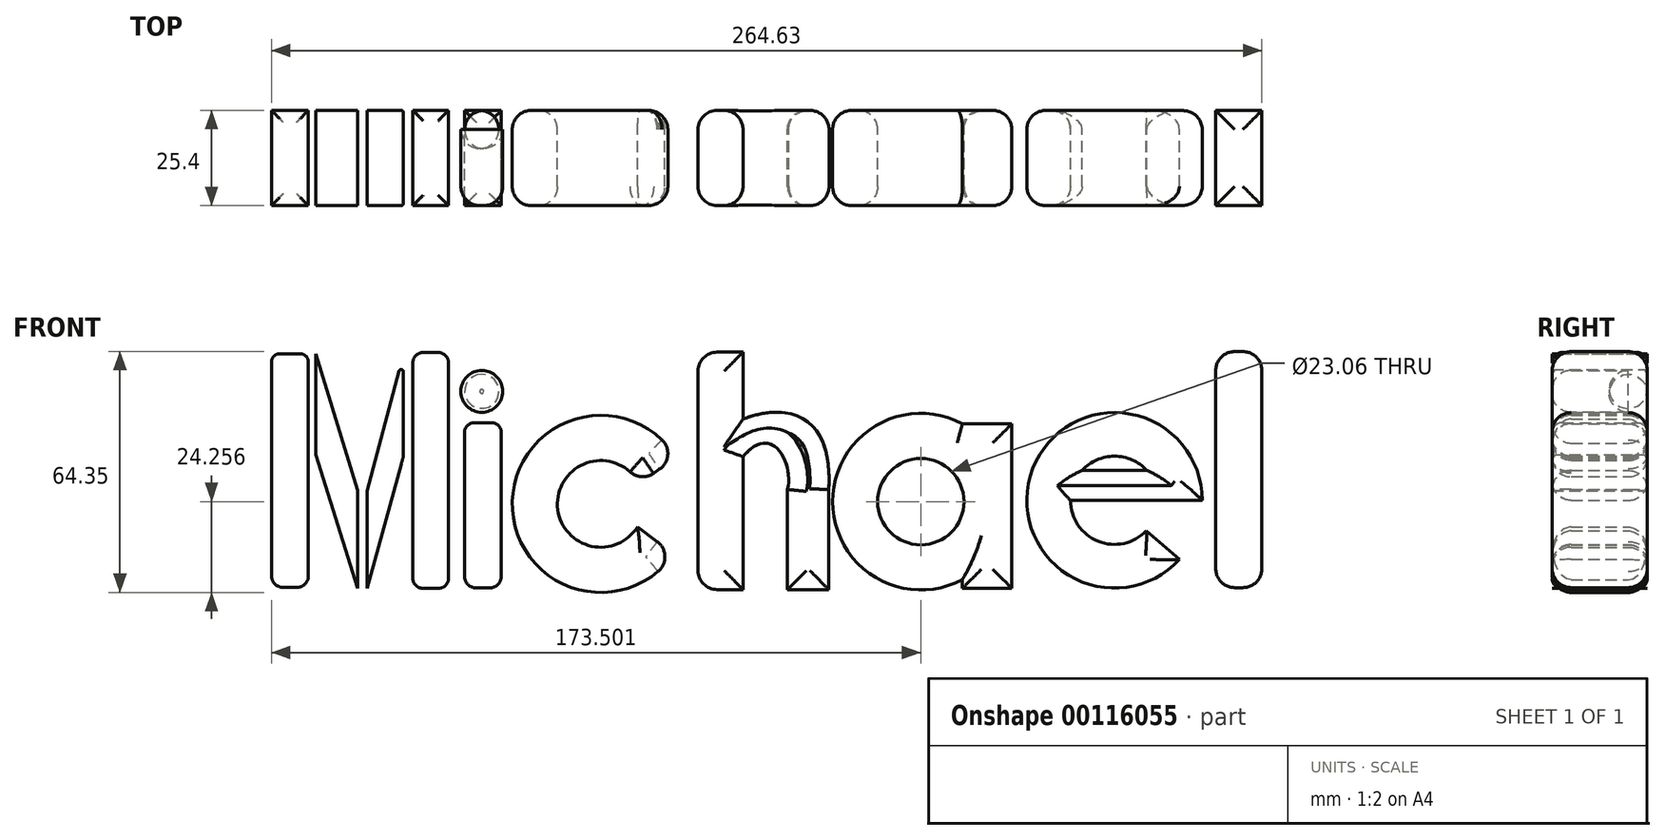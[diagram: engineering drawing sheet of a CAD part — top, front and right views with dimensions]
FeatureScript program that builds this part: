
annotation { "Feature Type Name" : "Feature", "Feature Type Description" : "" }
export const myFeature = defineFeature(function(context is Context, id is Id, definition is map)
    precondition{}
    {
        {
            var Q0;
            Q0=qCreatedBy(makeId("Front.planeOp"),FACE);
            var sketch = newSketch(context, id + "F0", { "sketchPlane" : qUnion([Q0])});
            skLineSegment(sketch, "E0.bottom", {"start": v(-141.21, 34.6) * mm, "end": v(141.21, 34.6) * mm});
            skLineSegment(sketch, "E0.top", {"start": v(-141.21, -34.6) * mm, "end": v(141.21, -34.6) * mm});
            skLineSegment(sketch, "E0.left", {"start": v(-141.21, 34.6) * mm, "end": v(-141.21, -34.6) * mm});
            skLineSegment(sketch, "E0.right", {"start": v(141.21, 34.6) * mm, "end": v(141.21, -34.6) * mm});
            skPoint(sketch, "E0.middle", {"position": v(0, 0) * mm});
            skLineSegment(sketch, "E1.bottom", {"start": v(-137.9, 31.16) * mm, "end": v(-128.02, 31.16) * mm});
            skLineSegment(sketch, "E1.top", {"start": v(-137.9, -31.25) * mm, "end": v(-128.02, -31.25) * mm});
            skLineSegment(sketch, "E1.left", {"start": v(-137.9, 31.16) * mm, "end": v(-137.9, -31.25) * mm});
            skLineSegment(sketch, "E1.right", {"start": v(-128.02, 31.16) * mm, "end": v(-128.02, -31.25) * mm});
            skLineSegment(sketch, "E2", {"start": v(-126.08, 31.16) * mm, "end": v(-126.08, 4.22) * mm});
            skLineSegment(sketch, "E3", {"start": v(-126.08, 4.22) * mm, "end": v(-114.84, -31.45) * mm});
            skLineSegment(sketch, "E4", {"start": v(-114.84, -31.45) * mm, "end": v(-114.84, -5.28) * mm});
            skLineSegment(sketch, "E5", {"start": v(-126.08, 31.16) * mm, "end": v(-114.84, -5.28) * mm});
            skLineSegment(sketch, "E6", {"start": v(-112.32, -31.45) * mm, "end": v(-112.32, -5.47) * mm});
            skLineSegment(sketch, "E7", {"start": v(-112.32, -5.47) * mm, "end": v(-102.62, 30.97) * mm});
            skLineSegment(sketch, "E8", {"start": v(-102.62, 30.97) * mm, "end": v(-102.62, 3.83) * mm});
            skLineSegment(sketch, "E9", {"start": v(-102.62, 3.83) * mm, "end": v(-112.32, -31.45) * mm});
            skLineSegment(sketch, "E10.bottom", {"start": v(-100.1, 31.55) * mm, "end": v(-90.6, 31.55) * mm});
            skLineSegment(sketch, "E10.top", {"start": v(-100.1, -31.45) * mm, "end": v(-90.6, -31.45) * mm});
            skLineSegment(sketch, "E10.left", {"start": v(-100.1, 31.55) * mm, "end": v(-100.1, -31.45) * mm});
            skLineSegment(sketch, "E10.right", {"start": v(-90.6, 31.55) * mm, "end": v(-90.6, -31.45) * mm});
            skLineSegment(sketch, "E11.bottom", {"start": v(-86.34, 12.78) * mm, "end": v(-76.46, 12.78) * mm});
            skLineSegment(sketch, "E11.top", {"start": v(-86.34, -31.42) * mm, "end": v(-76.46, -31.42) * mm});
            skLineSegment(sketch, "E11.left", {"start": v(-86.34, 12.78) * mm, "end": v(-86.34, -31.42) * mm});
            skLineSegment(sketch, "E11.right", {"start": v(-76.46, 12.78) * mm, "end": v(-76.46, -31.42) * mm});
            skCircle(sketch, "E12", {"center": v(-81.7, 21.11) * mm, "radius": 5.6 * mm});
            skCircle(sketch, "E13", {"center": v(-49.9, -8.93) * mm, "radius": 23.66 * mm});
            skCircle(sketch, "E14", {"center": v(-49.9, -8.93) * mm, "radius": 11.58 * mm});
            skLineSegment(sketch, "E15", {"start": v(-39.69, -3.48) * mm, "end": v(-29.72, 3.42) * mm});
            skLineSegment(sketch, "E16", {"start": v(-40.1, -15.1) * mm, "end": v(-30.38, -22.3) * mm});
            skLineSegment(sketch, "E17.bottom", {"start": v(-23.93, -31.8) * mm, "end": v(-11.9, -31.8) * mm});
            skLineSegment(sketch, "E17.top", {"start": v(-23.93, 31.58) * mm, "end": v(-11.9, 31.58) * mm});
            skLineSegment(sketch, "E17.left", {"start": v(-23.93, -31.8) * mm, "end": v(-23.93, 31.58) * mm});
            skLineSegment(sketch, "E17.right", {"start": v(-11.9, -31.8) * mm, "end": v(-11.9, 31.58) * mm});
            skLineSegment(sketch, "E18.bottom", {"start": v(0, -31.8) * mm, "end": v(11, -31.8) * mm});
            skLineSegment(sketch, "E18.top", {"start": v(0, -5.07) * mm, "end": v(11, -5.07) * mm});
            skLineSegment(sketch, "E18.left", {"start": v(0, -31.8) * mm, "end": v(0, -5.07) * mm});
            skLineSegment(sketch, "E18.right", {"start": v(11, -31.8) * mm, "end": v(11, -5.07) * mm});
            skFitSpline(sketch, "E19", {"points": [v(11, -5.07) * mm, v(-11.9, 13.72) * mm], "startDerivative": vector(3.34, 61.13) * mm, "endDerivative": vector(-35.7, -13.48) * mm});
            skFitSpline(sketch, "E20", {"points": [v(0, -5.07) * mm, v(-11.9, 3.67) * mm], "startDerivative": vector(4.92, 21.75) * mm, "endDerivative": vector(-23.05, -28.03) * mm});
            skCircle(sketch, "E21", {"center": v(35.6, -8.34) * mm, "radius": 23.58 * mm});
            skCircle(sketch, "E22", {"center": v(35.6, -8.34) * mm, "radius": 11.53 * mm});
            skLineSegment(sketch, "E23.bottom", {"start": v(46.7, 12.47) * mm, "end": v(59.92, 12.47) * mm});
            skLineSegment(sketch, "E23.top", {"start": v(46.7, -31.5) * mm, "end": v(59.92, -31.5) * mm});
            skLineSegment(sketch, "E23.left", {"start": v(46.7, 12.47) * mm, "end": v(46.7, -31.5) * mm});
            skLineSegment(sketch, "E23.right", {"start": v(59.92, 12.47) * mm, "end": v(59.92, -31.5) * mm});
            skCircle(sketch, "E24", {"center": v(87.35, -7.98) * mm, "radius": 23.44 * mm});
            skCircle(sketch, "E25", {"center": v(87.35, -7.98) * mm, "radius": 11.78 * mm});
            skLineSegment(sketch, "E26", {"start": v(75.57, -7.98) * mm, "end": v(99.13, -7.98) * mm});
            skLineSegment(sketch, "E27", {"start": v(78.7, 0) * mm, "end": v(96, 0) * mm});
            skLineSegment(sketch, "E28", {"start": v(99.13, -7.98) * mm, "end": v(110.79, -7.98) * mm});
            skLineSegment(sketch, "E29", {"start": v(95.87, -16.11) * mm, "end": v(104.67, -23.78) * mm});
            skLineSegment(sketch, "E30.bottom", {"start": v(114.39, -31.29) * mm, "end": v(126.73, -31.29) * mm});
            skLineSegment(sketch, "E30.top", {"start": v(114.39, 31.75) * mm, "end": v(126.73, 31.75) * mm});
            skLineSegment(sketch, "E30.left", {"start": v(114.39, -31.29) * mm, "end": v(114.39, 31.75) * mm});
            skLineSegment(sketch, "E30.right", {"start": v(126.73, -31.29) * mm, "end": v(126.73, 31.75) * mm});
            skSolve(sketch);
        }
        {
            var Q0;
            Q0=makeQuery(id+"F0.imprint","IMPRINT",FACE,{"disambiguationData":[TD([[makeQuery(id+"F0.imprint","IMPRINT",EDGE,{"derivedFrom":sQuery(id+"F0.wireOp",EDGE,"E1.bottom")}),-1.0]])]});
            var Q1;
            Q1=makeQuery(id+"F0.imprint","IMPRINT",FACE,{"disambiguationData":[TD([[makeQuery(id+"F0.imprint","IMPRINT",EDGE,{"derivedFrom":sQuery(id+"F0.wireOp",EDGE,"E2")}),1.0]])]});
            var Q2;
            Q2=makeQuery(id+"F0.imprint","IMPRINT",FACE,{"disambiguationData":[TD([[makeQuery(id+"F0.imprint","IMPRINT",EDGE,{"derivedFrom":sQuery(id+"F0.wireOp",EDGE,"E6")}),-1.0]])]});
            var Q3;
            Q3=makeQuery(id+"F0.imprint","IMPRINT",FACE,{"disambiguationData":[TD([[makeQuery(id+"F0.imprint","IMPRINT",EDGE,{"derivedFrom":sQuery(id+"F0.wireOp",EDGE,"E10.bottom")}),-1.0]])]});
            var Q4;
            Q4=makeQuery(id+"F0.imprint","IMPRINT",FACE,{"disambiguationData":[TD([[makeQuery(id+"F0.imprint","IMPRINT",EDGE,{"derivedFrom":sQuery(id+"F0.wireOp",EDGE,"E12")}),1.0]])]});
            var Q5;
            Q5=makeQuery(id+"F0.imprint","IMPRINT",FACE,{"disambiguationData":[TD([[makeQuery(id+"F0.imprint","IMPRINT",EDGE,{"derivedFrom":sQuery(id+"F0.wireOp",EDGE,"E11.bottom")}),-1.0]])]});
            var Q6;
            {var subQ0=sQuery(id+"F0.wireOp",EDGE,"E15");Q6=makeQuery(id+"F0.imprint","IMPRINT",FACE,{"disambiguationData":[TD([[makeQuery(id+"F0.imprint","IMPRINT",EDGE,{"derivedFrom":subQ0}),1.0]])]});}
            var Q7;
            {var subQ1=sQuery(id+"F0.wireOp",EDGE,"E17.bottom");Q7=makeQuery(id+"F0.imprint","IMPRINT",FACE,{"disambiguationData":[TD([[makeQuery(id+"F0.imprint","IMPRINT",EDGE,{"derivedFrom":subQ1}),1.0]])]});}
            var Q8;
            Q8=makeQuery(id+"F0.imprint","IMPRINT",FACE,{"disambiguationData":[TD([[makeQuery(id+"F0.imprint","IMPRINT",EDGE,{"derivedFrom":sQuery(id+"F0.wireOp",EDGE,"E18.top")}),1.0]])]});
            var Q9;
            Q9=makeQuery(id+"F0.imprint","IMPRINT",FACE,{"disambiguationData":[TD([[makeQuery(id+"F0.imprint","IMPRINT",EDGE,{"derivedFrom":sQuery(id+"F0.wireOp",EDGE,"E18.bottom")}),1.0]])]});
            var Q10;
            {var subQ0=sQuery(id+"F0.wireOp",EDGE,"E23.left");var subQ4=sQuery(id+"F0.wireOp",EDGE,"E22");var subQ5=makeQuery(id+"F0.imprint","INTERSECT",VERTEX,{"disambiguationData":[OD(0.0)],"derivedFrom":[subQ4,subQ0]});Q10=makeQuery(id+"F0.imprint","IMPRINT",FACE,{"disambiguationData":[TD([[makeQuery(id+"F0.imprint","IMPRINT",EDGE,{"disambiguationData":[TD([[subQ5,-1.0]])],"derivedFrom":subQ4}),-1.0]])]});}
            var Q11;
            {var subQ0=sQuery(id+"F0.wireOp",EDGE,"E23.left");var subQ4=sQuery(id+"F0.wireOp",EDGE,"E22");var subQ5=makeQuery(id+"F0.imprint","INTERSECT",VERTEX,{"disambiguationData":[OD(0.0)],"derivedFrom":[subQ4,subQ0]});Q11=makeQuery(id+"F0.imprint","IMPRINT",FACE,{"disambiguationData":[TD([[makeQuery(id+"F0.imprint","IMPRINT",EDGE,{"disambiguationData":[TD([[subQ5,1.0]])],"derivedFrom":subQ4}),-1.0]])]});}
            var Q12;
            {var subQ4=sQuery(id+"F0.wireOp",EDGE,"E23.bottom");Q12=makeQuery(id+"F0.imprint","IMPRINT",FACE,{"disambiguationData":[TD([[makeQuery(id+"F0.imprint","IMPRINT",EDGE,{"derivedFrom":subQ4}),-1.0]])]});}
            var Q13;
            {var subQ6=sQuery(id+"F0.wireOp",EDGE,"E28");Q13=makeQuery(id+"F0.imprint","IMPRINT",FACE,{"disambiguationData":[TD([[makeQuery(id+"F0.imprint","IMPRINT",EDGE,{"derivedFrom":subQ6}),1.0]])]});}
            var Q14;
            {var subQ0=sQuery(id+"F0.wireOp",EDGE,"E26");Q14=makeQuery(id+"F0.imprint","IMPRINT",FACE,{"disambiguationData":[TD([[makeQuery(id+"F0.imprint","IMPRINT",EDGE,{"derivedFrom":subQ0}),1.0]])]});}
            var Q15;
            Q15=makeQuery(id+"F0.imprint","IMPRINT",FACE,{"disambiguationData":[TD([[makeQuery(id+"F0.imprint","IMPRINT",EDGE,{"derivedFrom":sQuery(id+"F0.wireOp",EDGE,"E30.bottom")}),1.0]])]});
            extrude(context, id + "F1", {"entities" : qUnion([Q0, Q1, Q2, Q3, Q4, Q5, Q6, Q7, Q8, Q9, Q10, Q11, Q12, Q13, Q14, Q15]), "depth" : 25.4 * mm});
        }
        {
            var Q0;
            Q0=makeQuery(id+"F1.opExtrude","CAP_FACE",FACE,{"disambiguationData":[OSD([sQuery(id+"F0.wireOp",EDGE,"E12")])],"isStart":false});
            fillet(context, id + "F2", {"entities" : qUnion([Q0]), "radius" : 5.08 * mm, "tangentPropagation" : true, "allowEdgeOverflow" : false});
        }
        {
            var Q0;
            Q0=makeQuery(id+"F1.opExtrude","SWEPT_FACE",FACE,{"disambiguationData":[OSD([sQuery(id+"F0.wireOp",EDGE,"E13")])]});
            var Q1;
            Q1=makeQuery(id+"F1.opExtrude","CAP_FACE",FACE,{"disambiguationData":[OSD([sQuery(id+"F0.wireOp",EDGE,"E13"),sQuery(id+"F0.wireOp",EDGE,"E14"),sQuery(id+"F0.wireOp",EDGE,"E15"),sQuery(id+"F0.wireOp",EDGE,"E16")])],"isStart":false});
            var Q2;
            Q2=makeQuery(id+"F1.opExtrude","CAP_EDGE",EDGE,{"disambiguationData":[OSD([sQuery(id+"F0.wireOp",EDGE,"E13")])],"isStart":false});
            var Q3;
            Q3=makeQuery(id+"F1.opExtrude","CAP_FACE",FACE,{"disambiguationData":[OSD([sQuery(id+"F0.wireOp",EDGE,"E12")])],"isStart":true});
            fillet(context, id + "F3", {"entities" : qUnion([Q0, Q1, Q2, Q3]), "radius" : 5.08 * mm, "tangentPropagation" : true, "allowEdgeOverflow" : false});
        }
        {
            var Q0;
            Q0=makeQuery(id+"F3.opFillet","BLEND_FACE",FACE,{"disambiguationData":[OSD([sQuery(id+"F0.wireOp",EDGE,"E15")])]});
            var Q1;
            {var subQ0=sQuery(id+"F0.wireOp",EDGE,"E15");Q1=makeQuery(id+"F3.opFillet","BLEND_EDGE",EDGE,{"blendedFrom":[makeQuery(id+"F1.opExtrude","CAP_EDGE",EDGE,{"disambiguationData":[OSD([subQ0])],"isStart":false}),makeQuery(id+"F1.opExtrude","SWEPT_FACE",FACE,{"disambiguationData":[OSD([subQ0])]})],"blendedInto":[makeQuery(id+"F1.opExtrude","SWEPT_FACE",FACE,{"disambiguationData":[OSD([subQ0])]})]});}
            var Q2;
            Q2=makeQuery(id+"F1.opExtrude","SWEPT_FACE",FACE,{"disambiguationData":[OSD([sQuery(id+"F0.wireOp",EDGE,"E15")])]});
            var Q3;
            Q3=makeQuery(id+"F1.opExtrude","SWEPT_FACE",FACE,{"disambiguationData":[OSD([sQuery(id+"F0.wireOp",EDGE,"E17.left")])]});
            var Q4;
            Q4=makeQuery(id+"F1.opExtrude","CAP_FACE",FACE,{"disambiguationData":[OSD([sQuery(id+"F0.wireOp",EDGE,"E13"),sQuery(id+"F0.wireOp",EDGE,"E14"),sQuery(id+"F0.wireOp",EDGE,"E15"),sQuery(id+"F0.wireOp",EDGE,"E16")])],"isStart":true});
            var Q5;
            Q5=makeQuery(id+"F1.opExtrude","CAP_EDGE",EDGE,{"disambiguationData":[OSD([sQuery(id+"F0.wireOp",EDGE,"E15")])],"isStart":true});
            var Q6;
            Q6=makeQuery(id+"F1.opExtrude","CAP_FACE",FACE,{"disambiguationData":[OSD([sQuery(id+"F0.wireOp",EDGE,"E17.bottom"),sQuery(id+"F0.wireOp",EDGE,"E17.top"),sQuery(id+"F0.wireOp",EDGE,"E17.left"),sQuery(id+"F0.wireOp",EDGE,"E17.right"),sQuery(id+"F0.wireOp",EDGE,"E18.bottom"),sQuery(id+"F0.wireOp",EDGE,"E18.left"),sQuery(id+"F0.wireOp",EDGE,"E18.right"),sQuery(id+"F0.wireOp",EDGE,"E19"),sQuery(id+"F0.wireOp",EDGE,"E20")])],"isStart":true});
            var Q7;
            Q7=makeQuery(id+"F1.opExtrude","CAP_EDGE",EDGE,{"disambiguationData":[OSD([sQuery(id+"F0.wireOp",EDGE,"E17.left")])],"isStart":false});
            var Q8;
            Q8=makeQuery(id+"F1.opExtrude","CAP_EDGE",EDGE,{"disambiguationData":[OSD([sQuery(id+"F0.wireOp",EDGE,"E17.left")])],"isStart":true});
            var Q9;
            Q9=makeQuery(id+"F1.opExtrude","CAP_FACE",FACE,{"disambiguationData":[OSD([sQuery(id+"F0.wireOp",EDGE,"E17.bottom"),sQuery(id+"F0.wireOp",EDGE,"E17.top"),sQuery(id+"F0.wireOp",EDGE,"E17.left"),sQuery(id+"F0.wireOp",EDGE,"E17.right"),sQuery(id+"F0.wireOp",EDGE,"E18.bottom"),sQuery(id+"F0.wireOp",EDGE,"E18.left"),sQuery(id+"F0.wireOp",EDGE,"E18.right"),sQuery(id+"F0.wireOp",EDGE,"E19"),sQuery(id+"F0.wireOp",EDGE,"E20")])],"isStart":false});
            fillet(context, id + "F4", {"entities" : qUnion([Q0, Q1, Q2, Q3, Q4, Q5, Q6, Q7, Q8, Q9]), "radius" : 5.08 * mm, "tangentPropagation" : true, "allowEdgeOverflow" : false});
        }
        {
            var Q0;
            Q0=makeQuery(id+"F1.opExtrude","CAP_FACE",FACE,{"disambiguationData":[OSD([sQuery(id+"F0.wireOp",EDGE,"E21"),sQuery(id+"F0.wireOp",EDGE,"E22"),sQuery(id+"F0.wireOp",EDGE,"E23.bottom"),sQuery(id+"F0.wireOp",EDGE,"E23.top"),sQuery(id+"F0.wireOp",EDGE,"E23.left"),sQuery(id+"F0.wireOp",EDGE,"E23.right")])],"isStart":false});
            fillet(context, id + "F5", {"entities" : qUnion([Q0]), "radius" : 5.08 * mm, "tangentPropagation" : true, "allowEdgeOverflow" : false});
        }
        {
            var Q0;
            Q0=makeQuery(id+"F1.opExtrude","CAP_FACE",FACE,{"disambiguationData":[OSD([sQuery(id+"F0.wireOp",EDGE,"E24"),sQuery(id+"F0.wireOp",EDGE,"E25"),sQuery(id+"F0.wireOp",EDGE,"E26"),sQuery(id+"F0.wireOp",EDGE,"E27"),sQuery(id+"F0.wireOp",EDGE,"E28"),sQuery(id+"F0.wireOp",EDGE,"E29")])],"isStart":false});
            fillet(context, id + "F6", {"entities" : qUnion([Q0]), "radius" : 5.08 * mm, "tangentPropagation" : true, "allowEdgeOverflow" : false});
        }
        {
            var Q0;
            Q0=makeQuery(id+"F1.opExtrude","CAP_FACE",FACE,{"disambiguationData":[OSD([sQuery(id+"F0.wireOp",EDGE,"E21"),sQuery(id+"F0.wireOp",EDGE,"E22"),sQuery(id+"F0.wireOp",EDGE,"E23.bottom"),sQuery(id+"F0.wireOp",EDGE,"E23.top"),sQuery(id+"F0.wireOp",EDGE,"E23.left"),sQuery(id+"F0.wireOp",EDGE,"E23.right")])],"isStart":true});
            fillet(context, id + "F7", {"entities" : qUnion([Q0]), "radius" : 5.08 * mm, "tangentPropagation" : true, "allowEdgeOverflow" : false});
        }
        {
            var Q0;
            Q0=makeQuery(id+"F1.opExtrude","SWEPT_FACE",FACE,{"disambiguationData":[OSD([sQuery(id+"F0.wireOp",EDGE,"E30.top")])]});
            fillet(context, id + "F8", {"entities" : qUnion([Q0]), "radius" : 5.08 * mm, "tangentPropagation" : true, "allowEdgeOverflow" : false});
        }
        {
            var Q0;
            Q0=makeQuery(id+"F1.opExtrude","SWEPT_FACE",FACE,{"disambiguationData":[OSD([sQuery(id+"F0.wireOp",EDGE,"E30.bottom")])]});
            fillet(context, id + "F9", {"entities" : qUnion([Q0]), "radius" : 5.08 * mm, "tangentPropagation" : true, "allowEdgeOverflow" : false});
        }
        {
            var Q0;
            Q0=makeQuery(id+"F1.opExtrude","SWEPT_FACE",FACE,{"disambiguationData":[OSD([sQuery(id+"F0.wireOp",EDGE,"E1.top")])]});
            fillet(context, id + "F10", {"entities" : qUnion([Q0]), "radius" : 3.15 * mm, "tangentPropagation" : true, "allowEdgeOverflow" : false});
        }
        {
            var Q0;
            Q0=makeQuery(id+"F1.opExtrude","SWEPT_FACE",FACE,{"disambiguationData":[OSD([sQuery(id+"F0.wireOp",EDGE,"E10.top")])]});
            fillet(context, id + "F11", {"entities" : qUnion([Q0]), "radius" : 2.56 * mm, "tangentPropagation" : true, "allowEdgeOverflow" : false});
        }
        {
            var Q0;
            Q0=makeQuery(id+"F1.opExtrude","SWEPT_FACE",FACE,{"disambiguationData":[OSD([sQuery(id+"F0.wireOp",EDGE,"E10.bottom")])]});
            fillet(context, id + "F12", {"entities" : qUnion([Q0]), "radius" : 2.8 * mm, "tangentPropagation" : true, "allowEdgeOverflow" : false});
        }
        {
            var Q0;
            Q0=makeQuery(id+"F1.opExtrude","SWEPT_FACE",FACE,{"disambiguationData":[OSD([sQuery(id+"F0.wireOp",EDGE,"E1.bottom")])]});
            fillet(context, id + "F13", {"entities" : qUnion([Q0]), "radius" : 2.22 * mm, "tangentPropagation" : true, "allowEdgeOverflow" : false});
        }
        {
            var Q0;
            Q0=makeQuery(id+"F1.opExtrude","SWEPT_FACE",FACE,{"disambiguationData":[OSD([sQuery(id+"F0.wireOp",EDGE,"E11.bottom")])]});
            fillet(context, id + "F14", {"entities" : qUnion([Q0]), "radius" : 2.75 * mm, "tangentPropagation" : true, "allowEdgeOverflow" : false});
        }
        {
            var Q0;
            Q0=makeQuery(id+"F1.opExtrude","SWEPT_FACE",FACE,{"disambiguationData":[OSD([sQuery(id+"F0.wireOp",EDGE,"E11.top")])]});
            fillet(context, id + "F15", {"entities" : qUnion([Q0]), "radius" : 3.25 * mm, "tangentPropagation" : true, "allowEdgeOverflow" : false});
        }
        {
            var Q0;
            Q0=makeQuery(id+"F1.opExtrude","SWEPT_FACE",FACE,{"disambiguationData":[OSD([sQuery(id+"F0.wireOp",EDGE,"E8")])]});
            fillet(context, id + "F16", {"entities" : qUnion([Q0]), "radius" : 0.6 * mm, "tangentPropagation" : true, "allowEdgeOverflow" : false});
        }
        {
            var Q0;
            Q0=makeQuery(id+"F1.opExtrude","CAP_FACE",FACE,{"disambiguationData":[OSD([sQuery(id+"F0.wireOp",EDGE,"E24"),sQuery(id+"F0.wireOp",EDGE,"E25"),sQuery(id+"F0.wireOp",EDGE,"E26"),sQuery(id+"F0.wireOp",EDGE,"E27"),sQuery(id+"F0.wireOp",EDGE,"E28"),sQuery(id+"F0.wireOp",EDGE,"E29")])],"isStart":true});
            fillet(context, id + "F17", {"entities" : qUnion([Q0]), "radius" : 5.08 * mm, "tangentPropagation" : true, "allowEdgeOverflow" : false});
        }
    });
